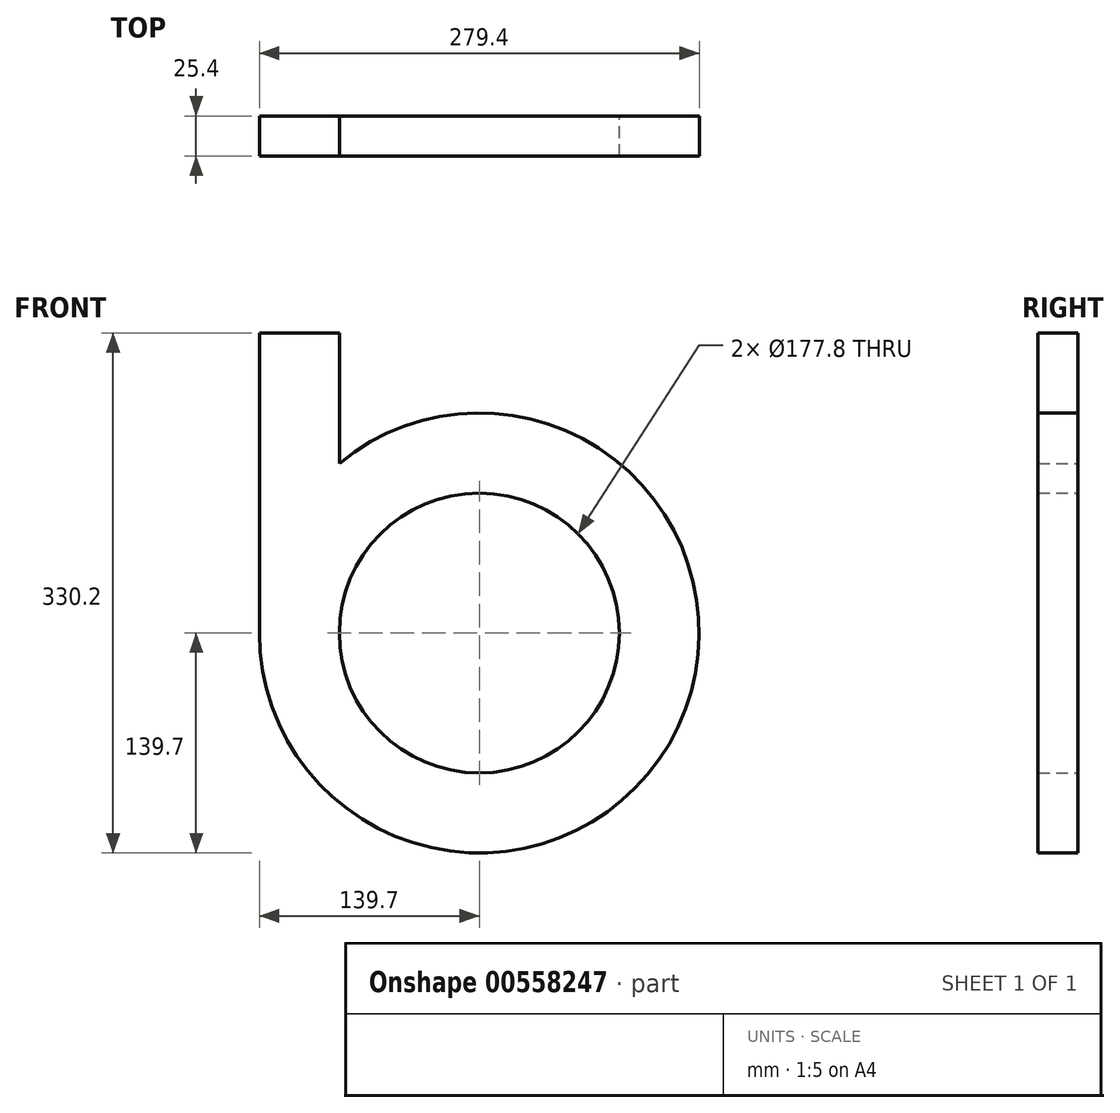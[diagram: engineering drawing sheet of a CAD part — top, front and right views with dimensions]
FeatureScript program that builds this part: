
annotation { "Feature Type Name" : "Feature", "Feature Type Description" : "" }
export const myFeature = defineFeature(function(context is Context, id is Id, definition is map)
    precondition{}
    {
        {
            var Q0;
            Q0=qCreatedBy(makeId("Front.planeOp"),FACE);
            var sketch = newSketch(context, id + "F0", { "sketchPlane" : qUnion([Q0])});
            skArc(sketch, "E0", {"start": v(-139.7, 0) * mm, "mid": v(126.36, -59.57) * mm, "end": v(-88.9, 107.76) * mm});
            skCircle(sketch, "E1", {"center": v(0, 0) * mm, "radius": 88.9 * mm});
            skLineSegment(sketch, "E2", {"start": v(-139.7, 0) * mm, "end": v(-139.7, 190.5) * mm});
            skLineSegment(sketch, "E3", {"start": v(-139.7, 190.5) * mm, "end": v(-88.9, 190.5) * mm});
            skLineSegment(sketch, "E4", {"start": v(-88.9, 190.5) * mm, "end": v(-88.9, 107.76) * mm});
            skSolve(sketch);
        }
        {
            var Q0;
            Q0 = qSketchRegion(id + "F0", true);
            extrude(context, id + "F1", {"entities" : qUnion([Q0]), "depth" : 25.4 * mm, "offsetDistance" : 25.4 * mm});
        }
    });
